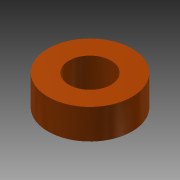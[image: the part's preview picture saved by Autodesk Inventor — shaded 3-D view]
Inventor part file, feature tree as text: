
AUTODESK INVENTOR PART (.ipt)
format: ipt  version: 2013 (Build 170138000, 138)  size: 75,776 bytes
history: native  units: mm
features: extrude x1, sketch x1
ambient origin geometry x8: Origin, YZ Plane, XZ Plane, XY Plane, X Axis, Y Axis, Z Axis, Center Point
bodies: Solid1 (feature_tree)
feature tree (2):
  extrude  "Extrusion1"  Depth=5.25mm
  sketch  "Sketch1"  dims[d0=10.5mm d3=5.25mm d4=3.75mm d5=0.0mm]
